# Revit family: ВентКлиматСтрой Вентилятор канальный ВРПП
name_source: partatom
category: Оборудование
units: mm (PartAtom-declared; Revit-internal decimal feet)

## family parameters
Всегда вертикально = Нет
Заголовок OmniClass = Fans for Air Ductwork
На основе рабочей плоскости = Нет
Номер OmniClass = 23.75.35.17.11
Общий = Нет
При загрузке вырезать с полостями = Нет
Размер круглого соединителя = Использовать диаметр
Тип детали = Вставляется
Точка расчета площади = Нет

## types (9) — shared parameters
ADSK_Версия Revit = 2019
ADSK_Версия семейства = rev.1
ADSK_Единица измерения = шт.
ADSK_Завод-изготовитель = ООО "ЗВО ВентКлиматСтрой"
ADSK_Классификация нагрузок = Прочее
ADSK_Количество фаз = 3
BT = 5 мм
Data = ВРПП
Rin = 100 мм
Rin1 = 98 мм
T = 5 мм
f = 20 мм
Клеммная коробка = Да
zero-valued in all types: ADSK_Материал тип подсчета

## per-type parameters (varying)
| type | A | A1 | A2 | B | B1 | B2 | D | D1 | H | L | L1 | Lb | RinAng |
| ВРПП-30x15* | 300 мм | 320 мм | 340 мм | 150 мм | 170 мм | 190 мм | 150 мм | 150 мм | 220 мм | 380 мм | 180 мм | 370 мм | 15.00° |
| ВРПП-40x20* | 400 мм | 420 мм | 440 мм | 200 мм | 220 мм | 240 мм | 200 мм | 200 мм | 270 мм | 400 мм | 191 мм | 390 мм | 30.00° |
| ВРПП-50x25* | 500 мм | 520 мм | 540 мм | 250 мм | 270 мм | 290 мм | 250 мм | 230 мм | 300 мм | 480 мм | 232 мм | 470 мм | 45.00° |
| ВРПП-50x30* | 500 мм | 520 мм | 540 мм | 300 мм | 320 мм | 340 мм | 300 мм | 280 мм | 340 мм | 500 мм | 243 мм | 490 мм | 45.00° |
| ВРПП-60x30* | 600 мм | 620 мм | 640 мм | 300 мм | 320 мм | 340 мм | 300 мм | 280 мм | 340 мм | 500 мм | 243 мм | 490 мм | 45.00° |
| ВРПП-60x35* | 600 мм | 620 мм | 640 мм | 350 мм | 370 мм | 390 мм | 350 мм | 330 мм | 390 мм | 580 мм | 284 мм | 570 мм | 45.00° |
| ВРПП-70x40* | 700 мм | 720 мм | 740 мм | 400 мм | 420 мм | 440 мм | 400 мм | 380 мм | 440 мм | 580 мм | 284 мм | 570 мм | 45.00° |
| ВРПП-80x50* | 800 мм | 830 мм | 860 мм | 500 мм | 530 мм | 560 мм | 500 мм | 480 мм | 560 мм | 650 мм | 317 мм | 640 мм | 75.00° |
| ВРПП-100x50* | 1000 мм | 1030 мм | 1060 мм | 500 мм | 530 мм | 560 мм | 500 мм | 480 мм | 560 мм | 725 мм | 356 мм | 715 мм | 75.00° |
